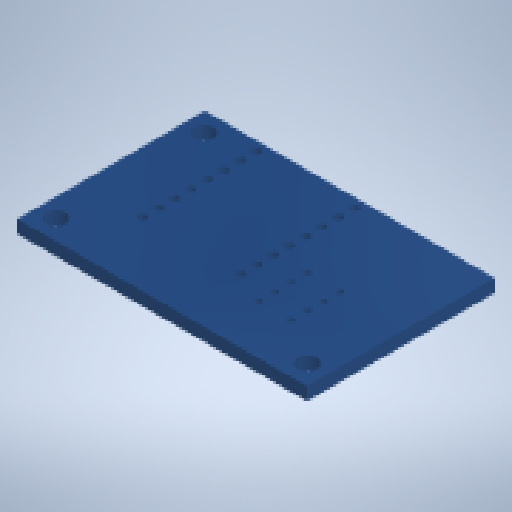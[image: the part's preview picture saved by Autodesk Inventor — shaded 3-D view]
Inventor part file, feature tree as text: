
AUTODESK INVENTOR PART (.ipt)
format: ipt  version: 2024 (Build 280153000, 153)  size: 786,944 bytes
history: native  units: mm
features: other x26, extrude x1, sketch x1, projected_geometry x1
ambient origin geometry x8: Origin, YZ Plane, XZ Plane, XY Plane, X Axis, Y Axis, Z Axis, Center Point
bodies: Volumenkörper1 (feature_tree), Volumenkörper2 (feature_tree), Volumenkörper3 (feature_tree), Volumenkörper4 (feature_tree), Volumenkörper5 (feature_tree), Volumenkörper6 (feature_tree), Volumenkörper7 (feature_tree), Volumenkörper8 (feature_tree), Volumenkörper9 (feature_tree), Volumenkörper10 (feature_tree), Volumenkörper11 (feature_tree), Volumenkörper12 (feature_tree), Volumenkörper13 (feature_tree), Volumenkörper14 (feature_tree), Volumenkörper15 (feature_tree), Volumenkörper16 (feature_tree), Volumenkörper17 (feature_tree), Volumenkörper18 (feature_tree), Volumenkörper19 (feature_tree), Volumenkörper20 (feature_tree), Volumenkörper21 (feature_tree), Volumenkörper22 (feature_tree), Volumenkörper23 (feature_tree), Volumenkörper24 (feature_tree), Volumenkörper25 (feature_tree), Volumenkörper26 (feature_tree)
feature tree (29):
  extrude  "Extrusion1"  [1 undecoded]
  sketch  "Skizze1"  dims[d0=1.589mm d1=0.0mm]
  projected_geometry  "Projizierte Kontur1"
  other  "Open CASCADE STEP translator 7.5 3.1.1_15:1"
  other  "Board c3mini_17:1"
  other  "Board c3mini_17:2"
  other  "Board c3mini_17:3"
  other  "Board c3mini_17:4"
  other  "Board c3mini_17:5"
  other  "Board c3mini_17:6"
  other  "Board c3mini_17:7"
  other  "Board c3mini_17:8"
  other  "Board c3mini_17:9"
  other  "Board c3mini_17:10"
  other  "Board c3mini_17:11"
  other  "Board c3mini_17:12"
  other  "Board c3mini_17:13"
  other  "Board c3mini_17:14"
  other  "Board c3mini_17:15"
  other  "Board c3mini_17:16"
  other  "Board c3mini_17:17"
  other  "USB C_18:1"
  other  "components (other)^ESP32-C3 SuperMini_19:1"
  other  "components (other)^ESP32-C3 SuperMini_19:2"
  other  "components (other)^ESP32-C3 SuperMini_19:3"
  other  "components (other)^ESP32-C3 SuperMini_19:4"
  other  "components (other)^ESP32-C3 SuperMini_19:5"
  other  "components (other)^ESP32-C3 SuperMini_19:6"
  other  "components (other)^ESP32-C3 SuperMini_19:7"
note: 1 required parameter value undecoded (feature->parameter linkage not recoverable at this tier; creation-order binding heuristic only, values carry confidence <= 0.55)
